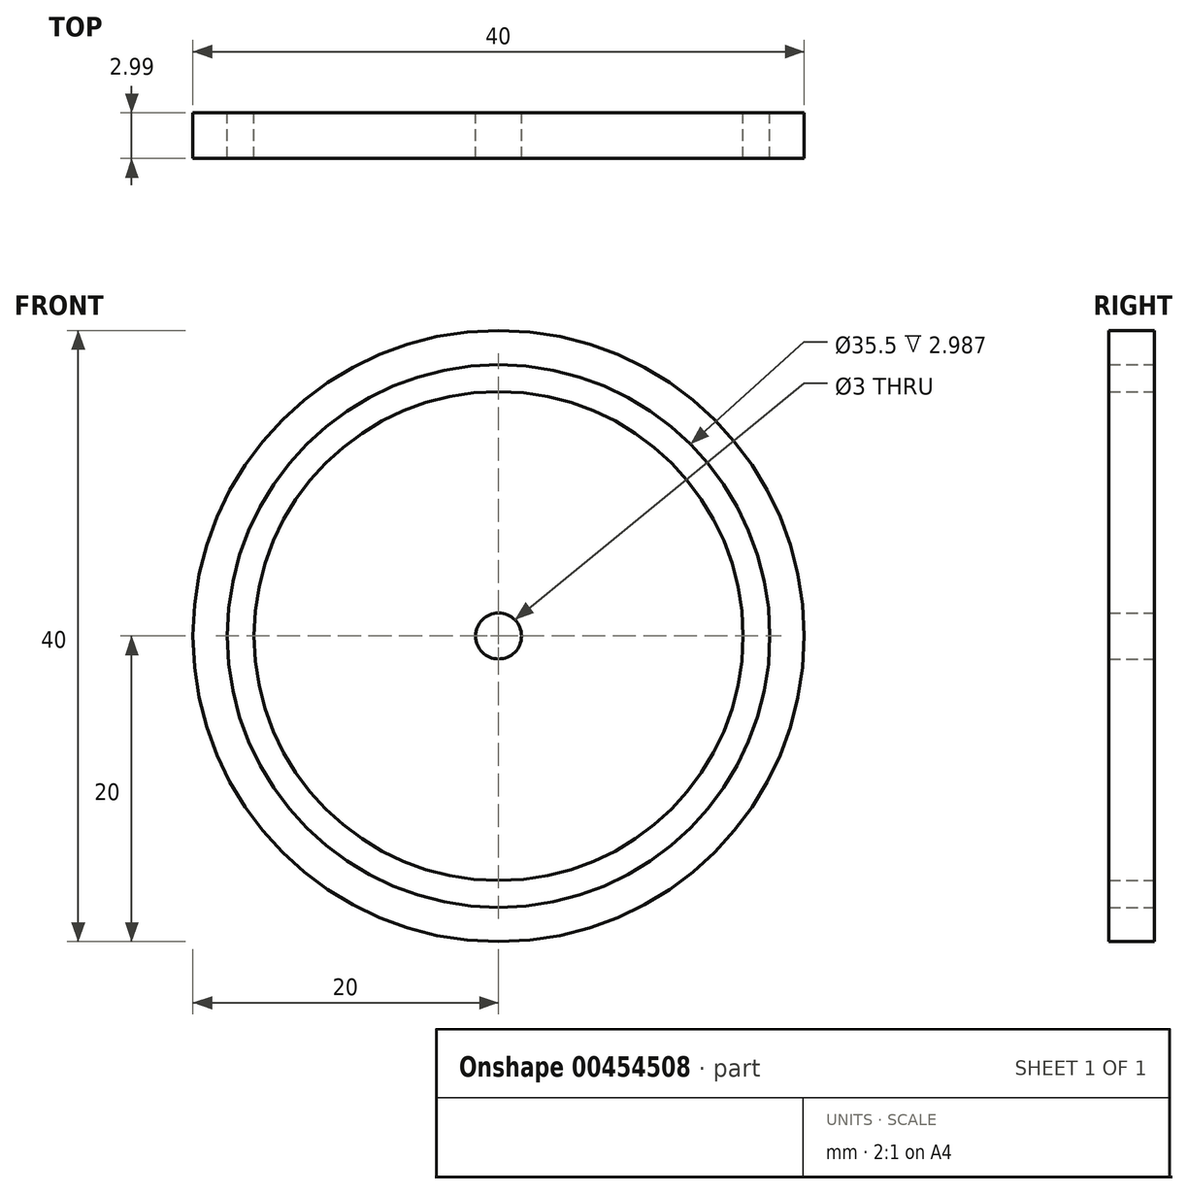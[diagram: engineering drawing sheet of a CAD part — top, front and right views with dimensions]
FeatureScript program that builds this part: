
annotation { "Feature Type Name" : "Feature", "Feature Type Description" : "" }
export const myFeature = defineFeature(function(context is Context, id is Id, definition is map)
    precondition{}
    {
        {
            var Q0;
            Q0=qCreatedBy(makeId("Front.planeOp"),FACE);
            var sketch = newSketch(context, id + "F0", { "sketchPlane" : qUnion([Q0])});
            skCircle(sketch, "E0", {"center": v(0, 0) * mm, "radius": 20 * mm});
            skCircle(sketch, "E1", {"center": v(0, 0) * mm, "radius": 17.75 * mm});
            skCircle(sketch, "E2", {"center": v(0, 0) * mm, "radius": 16 * mm});
            skCircle(sketch, "E3", {"center": v(0, 0) * mm, "radius": 3 * mm});
            skCircle(sketch, "E4", {"center": v(0, 0) * mm, "radius": 1.5 * mm});
            skLineSegment(sketch, "E5", {"start": v(0, 34.59) * mm, "end": v(0, -51.24) * mm, "construction": true});
            skLineSegment(sketch, "E6", {"start": v(-50.76, 0) * mm, "end": v(48.89, 0) * mm, "construction": true});
            skSolve(sketch);
        }
        {
            var Q0;
            Q0 = qSketchRegion(id + "F0", true);
            var Q1;
            Q1=makeQuery(id+"F0.imprint","IMPRINT",FACE,{"disambiguationData":[TD([[makeQuery(id+"F0.imprint","IMPRINT",EDGE,{"derivedFrom":sQuery(id+"F0.wireOp",EDGE,"E3")}),1.0]])]});
            var Q2;
            Q2=makeQuery(id+"F0.imprint","IMPRINT",FACE,{"disambiguationData":[TD([[makeQuery(id+"F0.imprint","IMPRINT",EDGE,{"derivedFrom":sQuery(id+"F0.wireOp",EDGE,"E2")}),1.0]])]});
            extrude(context, id + "F1", {"entities" : qUnion([Q0, Q1, Q2]), "depth" : 3 * mm});
        }
    });
